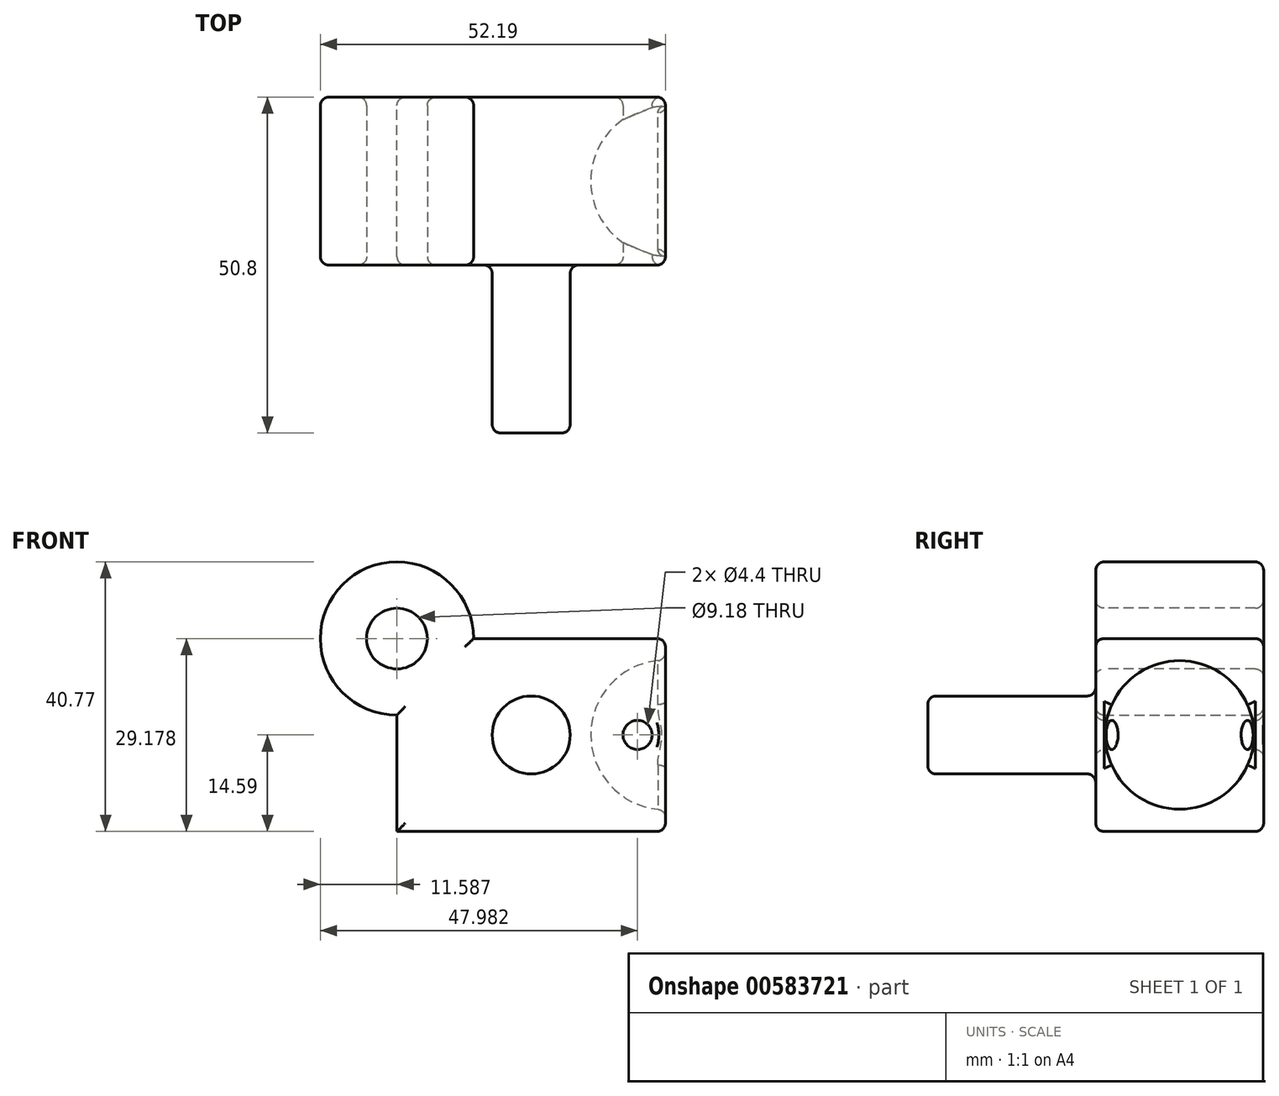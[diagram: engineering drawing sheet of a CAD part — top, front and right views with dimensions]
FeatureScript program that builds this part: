
annotation { "Feature Type Name" : "Feature", "Feature Type Description" : "" }
export const myFeature = defineFeature(function(context is Context, id is Id, definition is map)
    precondition{}
    {
        {
            var Q0;
            Q0=qCreatedBy(makeId("Front.planeOp"),FACE);
            var sketch = newSketch(context, id + "F0", { "sketchPlane" : qUnion([Q0])});
            skLineSegment(sketch, "E0.bottom", {"start": v(-20.3, 14.59) * mm, "end": v(20.3, 14.59) * mm});
            skLineSegment(sketch, "E0.top", {"start": v(-20.3, -14.59) * mm, "end": v(20.3, -14.59) * mm});
            skLineSegment(sketch, "E0.left", {"start": v(-20.3, 14.59) * mm, "end": v(-20.3, -14.59) * mm});
            skLineSegment(sketch, "E0.right", {"start": v(20.3, 14.59) * mm, "end": v(20.3, -14.59) * mm});
            skPoint(sketch, "E0.middle", {"position": v(0, 0) * mm});
            skCircle(sketch, "E1", {"center": v(-20.3, 14.59) * mm, "radius": 11.6 * mm});
            skSolve(sketch);
        }
        {
            var Q0;
            {var subQ2=sQuery(id+"F0.wireOp",EDGE,"E0.top");Q0=makeQuery(id+"F0.imprint","IMPRINT",FACE,{"disambiguationData":[TD([[makeQuery(id+"F0.imprint","IMPRINT",EDGE,{"derivedFrom":subQ2}),1.0]])]});}
            var Q1;
            {var subQ0=sQuery(id+"F0.wireOp",EDGE,"E0.left");var subQ1=sQuery(id+"F0.wireOp",EDGE,"E0.bottom");var subQ2=makeQuery(id+"F0.imprint","INTERSECT",VERTEX,{"derivedFrom":[subQ1,subQ0]});Q1=makeQuery(id+"F0.imprint","IMPRINT",FACE,{"disambiguationData":[TD([[makeQuery(id+"F0.imprint","IMPRINT",EDGE,{"disambiguationData":[TD([[subQ2,-1.0]])],"derivedFrom":subQ1}),1.0]])]});}
            var Q2;
            {var subQ0=sQuery(id+"F0.wireOp",EDGE,"E0.left");var subQ1=sQuery(id+"F0.wireOp",EDGE,"E0.bottom");var subQ2=makeQuery(id+"F0.imprint","INTERSECT",VERTEX,{"derivedFrom":[subQ1,subQ0]});Q2=makeQuery(id+"F0.imprint","IMPRINT",FACE,{"disambiguationData":[TD([[makeQuery(id+"F0.imprint","IMPRINT",EDGE,{"disambiguationData":[TD([[subQ2,-1.0]])],"derivedFrom":subQ1}),-1.0]])]});}
            extrude(context, id + "F1", {"entities" : qUnion([Q0, Q1, Q2]), "endBound" : BoundingType.SYMMETRIC, "depth" : 25.4 * mm, "offsetDistance" : 25.4 * mm});
        }
        {
            var Q0;
            Q0=makeQuery(id+"F1.opExtrude","CAP_FACE",FACE,{"disambiguationData":[OSD([sQuery(id+"F0.wireOp",EDGE,"E0.bottom"),sQuery(id+"F0.wireOp",EDGE,"E0.top"),sQuery(id+"F0.wireOp",EDGE,"E0.left"),sQuery(id+"F0.wireOp",EDGE,"E0.right"),sQuery(id+"F0.wireOp",EDGE,"E1")])],"isStart":false});
            var sketch = newSketch(context, id + "F2", { "sketchPlane" : qUnion([Q0])});
            skCircle(sketch, "E2", {"center": v(-20.3, 14.59) * mm, "radius": 4.6 * mm});
            skSolve(sketch);
        }
        {
            var Q0;
            Q0=makeQuery(id+"F2.imprint","IMPRINT",FACE,{"disambiguationData":[TD([[makeQuery(id+"F2.imprint","IMPRINT",EDGE,{"derivedFrom":sQuery(id+"F2.wireOp",EDGE,"E2")}),1.0]])]});
            var Q1;
            Q1=sQuery(id+"F2.wireOp",EDGE,"E2");
            extrude(context, id + "F3", {"entities" : qUnion([Q0]), "operationType" : NewBodyOperationType.REMOVE, "surfaceEntities" : qUnion([Q1]), "oppositeDirection" : true, "depth" : 25.4 * mm, "offsetDistance" : 25.4 * mm});
        }
        {
            var Q0;
            Q0=makeQuery(id+"F1.opExtrude","CAP_FACE",FACE,{"disambiguationData":[OSD([sQuery(id+"F0.wireOp",EDGE,"E0.bottom"),sQuery(id+"F0.wireOp",EDGE,"E0.top"),sQuery(id+"F0.wireOp",EDGE,"E0.left"),sQuery(id+"F0.wireOp",EDGE,"E0.right"),sQuery(id+"F0.wireOp",EDGE,"E1")])],"isStart":false});
            var sketch = newSketch(context, id + "F4", { "sketchPlane" : qUnion([Q0])});
            skCircle(sketch, "E3", {"center": v(0, 0) * mm, "radius": 5.9 * mm});
            skSolve(sketch);
        }
        {
            var Q0;
            Q0=makeQuery(id+"F4.imprint","IMPRINT",FACE,{"disambiguationData":[TD([[makeQuery(id+"F4.imprint","IMPRINT",EDGE,{"derivedFrom":sQuery(id+"F4.wireOp",EDGE,"E3")}),1.0]])]});
            extrude(context, id + "F5", {"entities" : qUnion([Q0]), "operationType" : NewBodyOperationType.ADD, "depth" : 25.4 * mm, "offsetDistance" : 25.4 * mm});
        }
        {
            var Q0;
            Q0=qCreatedBy(makeId("Front.planeOp"),FACE);
            var sketch = newSketch(context, id + "F6", { "sketchPlane" : qUnion([Q0])});
            skCircle(sketch, "E4", {"center": v(20.3, 0) * mm, "radius": 11.3 * mm});
            skLineSegment(sketch, "E5", {"start": v(20.3, 23.61) * mm, "end": v(20.3, -28.42) * mm});
            skSolve(sketch);
        }
        {
            var Q0;
            {var subQ0=sQuery(id+"F6.wireOp",EDGE,"E5");var subQ1=sQuery(id+"F6.wireOp",EDGE,"E4");var subQ2=makeQuery(id+"F6.imprint","INTERSECT",VERTEX,{"disambiguationData":[OD(0.0)],"derivedFrom":[subQ1,subQ0]});Q0=makeQuery(id+"F6.imprint","IMPRINT",FACE,{"disambiguationData":[TD([[makeQuery(id+"F6.imprint","IMPRINT",EDGE,{"disambiguationData":[TD([[subQ2,1.0]])],"derivedFrom":subQ1}),1.0]])]});}
            var Q1;
            Q1=sQuery(id+"F6.wireOp",EDGE,"E5");
            revolve(context, id + "F7", {"entities" : qUnion([Q0]), "axis" : qUnion([Q1]), "revolveType" : RevolveType.FULL});
        }
        {
            var Q0;
            Q0=makeQuery(id+"F7.opRevolve","SWEPT_BODY",BODY,{"disambiguationData":[OSD([sQuery(id+"F6.wireOp",EDGE,"E4"),sQuery(id+"F6.wireOp",EDGE,"E5")])]});
            var Q1;
            Q1=makeQuery(id+"F1.opExtrude","SWEPT_BODY",BODY,{"disambiguationData":[OSD([sQuery(id+"F0.wireOp",EDGE,"E0.bottom"),sQuery(id+"F0.wireOp",EDGE,"E0.top"),sQuery(id+"F0.wireOp",EDGE,"E0.left"),sQuery(id+"F0.wireOp",EDGE,"E0.right"),sQuery(id+"F0.wireOp",EDGE,"E1")])]});
            booleanBodies(context, id + "F8", {"operationType" : BooleanOperationType.SUBTRACTION, "tools" : qUnion([Q0]), "targets" : qUnion([Q1])});
        }
        {
            var Q0;
            Q0=makeQuery(id+"F1.opExtrude","CAP_FACE",FACE,{"disambiguationData":[OSD([sQuery(id+"F0.wireOp",EDGE,"E0.bottom"),sQuery(id+"F0.wireOp",EDGE,"E0.top"),sQuery(id+"F0.wireOp",EDGE,"E0.left"),sQuery(id+"F0.wireOp",EDGE,"E0.right"),sQuery(id+"F0.wireOp",EDGE,"E1")])],"isStart":false});
            var sketch = newSketch(context, id + "F9", { "sketchPlane" : qUnion([Q0])});
            skPoint(sketch, "E6", {"position": v(16.1, 0) * mm});
            skPoint(sketch, "E6.positionSnap0", {"position": v(20.3, 0) * mm});
            skSolve(sketch);
        }
        {
            var Q0;
            Q0=sQuery(id+"F9.wireOp",VERTEX,"E6");
            var Q1;
            Q1=makeQuery(id+"F1.opExtrude","SWEPT_BODY",BODY,{"disambiguationData":[OSD([sQuery(id+"F0.wireOp",EDGE,"E0.bottom"),sQuery(id+"F0.wireOp",EDGE,"E0.top"),sQuery(id+"F0.wireOp",EDGE,"E0.left"),sQuery(id+"F0.wireOp",EDGE,"E0.right"),sQuery(id+"F0.wireOp",EDGE,"E1")])]});
            hole(context, id + "F10", {"style" : HoleStyle.SIMPLE, "endStyle" : HoleEndStyle.THROUGH, "standardTappedOrClearance" : lookupTablePath({ "standard" : "ISO", "fit" : "Normal", "size" : "M4", "type" : "Clearance" }), "standardBlindInLast" : lookupTablePath({ "fit" : "Standard", "standard" : "ISO", "size" : "M4", "type" : "Clearance" }), "holeDiameter" : 4.4 * mm, "majorDiameter" : 6.35 * mm, "isTappedThrough" : true, "tappedDepth" : 12.7 * mm, "tapClearance" : 3, "startFromSketch" : true, "locations" : qUnion([Q0]), "scope" : qUnion([Q1])});
        }
        {
            var Q0;
            Q0=makeQuery(id+"F5.opExtrude","CAP_FACE",FACE,{"disambiguationData":[OSD([sQuery(id+"F4.wireOp",EDGE,"E3")])],"isStart":false});
            fillet(context, id + "F11", {"entities" : qUnion([Q0]), "radius" : 1.27 * mm, "tangentPropagation" : true, "allowEdgeOverflow" : false});
        }
        {
            var Q0;
            Q0=makeQuery(id+"F1.opExtrude","CAP_FACE",FACE,{"disambiguationData":[OSD([sQuery(id+"F0.wireOp",EDGE,"E0.bottom"),sQuery(id+"F0.wireOp",EDGE,"E0.top"),sQuery(id+"F0.wireOp",EDGE,"E0.left"),sQuery(id+"F0.wireOp",EDGE,"E0.right"),sQuery(id+"F0.wireOp",EDGE,"E1")])],"isStart":false});
            fillet(context, id + "F12", {"entities" : qUnion([Q0]), "radius" : 1.27 * mm, "tangentPropagation" : true, "allowEdgeOverflow" : false});
        }
        {
            var Q0;
            Q0=makeQuery(id+"F1.opExtrude","CAP_FACE",FACE,{"disambiguationData":[OSD([sQuery(id+"F0.wireOp",EDGE,"E0.bottom"),sQuery(id+"F0.wireOp",EDGE,"E0.top"),sQuery(id+"F0.wireOp",EDGE,"E0.left"),sQuery(id+"F0.wireOp",EDGE,"E0.right"),sQuery(id+"F0.wireOp",EDGE,"E1")])],"isStart":true});
            fillet(context, id + "F13", {"entities" : qUnion([Q0]), "radius" : 1.27 * mm, "tangentPropagation" : true, "allowEdgeOverflow" : false});
        }
        {
            var Q0;
            Q0=makeQuery(id+"F1.opExtrude","SWEPT_FACE",FACE,{"disambiguationData":[OSD([sQuery(id+"F0.wireOp",EDGE,"E0.right")])]});
            fillet(context, id + "F14", {"entities" : qUnion([Q0]), "radius" : 1.27 * mm, "tangentPropagation" : true, "allowEdgeOverflow" : false});
        }
    });
